# Revit family: Basin-Wall-Caroma Teo 410 Vanity
name_source: partatom
category: Plumbing Fixtures
revit_build: Autodesk Revit 2014 (Build: 20131024_2115(x64)
units: mm (PartAtom-declared; Revit-internal decimal feet)

## types (1)
- Teo 410 - 1 Tap Hole
    1 Taphole = Yes
    3 Tapholes = No
    Assembly Code = D2010310
    CW Connection = No
    Capacity_ANZRS = 3.8 L
    Default Elevation = 865 mm  [stored 2.83793 ft]
    Description = Caroma Teo 410 Wall Basin
    HW Connection = No
    Height_ANZRS = 140 mm  [stored 0.459318 ft]
    Length_ANZRS = 415 mm  [stored 1.36155 ft]
    Manufacturer = GWA Bathrooms & Kitchens
    Material_ANZRS = Porcelain-White-Caroma
    Model = EU8031A10
    ModifiedIssue_ANZRS = 20141103.01 $
    Spout Penetration = 0 mm  [stored 0 ft]
    Tap Penetrations = 100 mm  [stored 0.328084 ft]
    Type Comments = White Only, Overflow not available, Chrome flush fitting waste and white plug supplied
    URL = http://www.caroma.com.au
    Vent Connection = No
    WFU = 1
    Waste = Metal-Chrome-Caroma
    Waste Connection = Yes
    WasteOutlet_ANZRS = 0
    Width_ANZRS = 235 mm  [stored 0.770997 ft]

note: [stored X ft] marks values corroborated as IEEE doubles in the binary element streams (Revit-internal decimal feet)

## geometry (parser evidence)
native form markers: Blend x12, Sweep x3
no freeform markers — native parametric forms only
